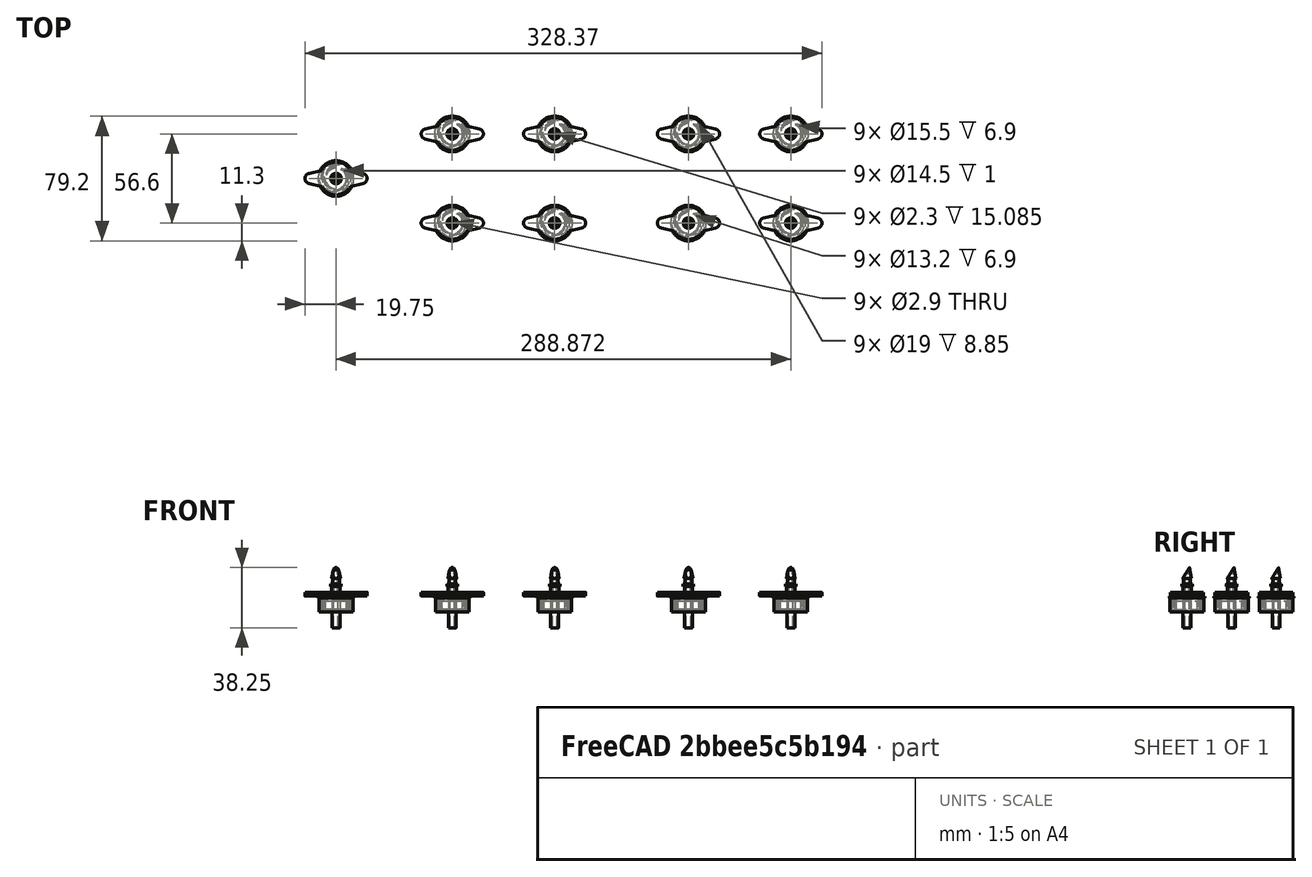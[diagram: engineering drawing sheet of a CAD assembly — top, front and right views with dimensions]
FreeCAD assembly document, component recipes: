
FREECAD ASSEMBLY — COMPONENT RECIPES ("composit_stand3_dropper_fix_assembly")

This assembly document has 2 components, labeled P0..P1 below (a component is one placed body or linked part). 0 of them carry a construction recipe — the FreeCAD feature program that regenerates the part from scratch, quoted from this document or its linked companion documents; the rest are supplied as boundary geometry only. No exploded tour is included for this assembly.
COMPONENT P0 — geometry summary ("Assembly"; no construction recipe available for this part):
  bounding box: 351.9 x 90.2 x 58.5 mm
  tessellated surface: 6,304 triangles
  volume: 482995144076382510045496328185634469381367029842250084827643351265021887885973797658214928087502553088 mm^3 (26013343870852097516416644482389625382723460628132650615000746128420575062207036003034043760246784% of its bounding box)
  symmetry: mirror-symmetric across its y mid-plane
COMPONENT P1 — geometry summary ("droppers"; no construction recipe available for this part):
  bounding box: 254.5 x 79.2 x 38.2 mm
  tessellated surface: 2,976 triangles
  volume: 53241681557722748069024161879179496356513765836130727964224679202593699705244553484154046846884380672 mm^3 (6915610360425659975807596399796662615641554874222959956707919953453755673324267103853481461547008% of its bounding box)
  symmetry: 2-fold rotationally symmetric about the z axis; mirror-symmetric across its x mid-plane, y mid-plane
PROVENANCE & LICENSES
A FreeCAD (.FCStd) document from a public repository crawl; recipes are the document's own serialized feature recipes (and, for linked parts, companion documents' recipes).
License: as declared in the source repository (recorded in the dataset sidecar).
